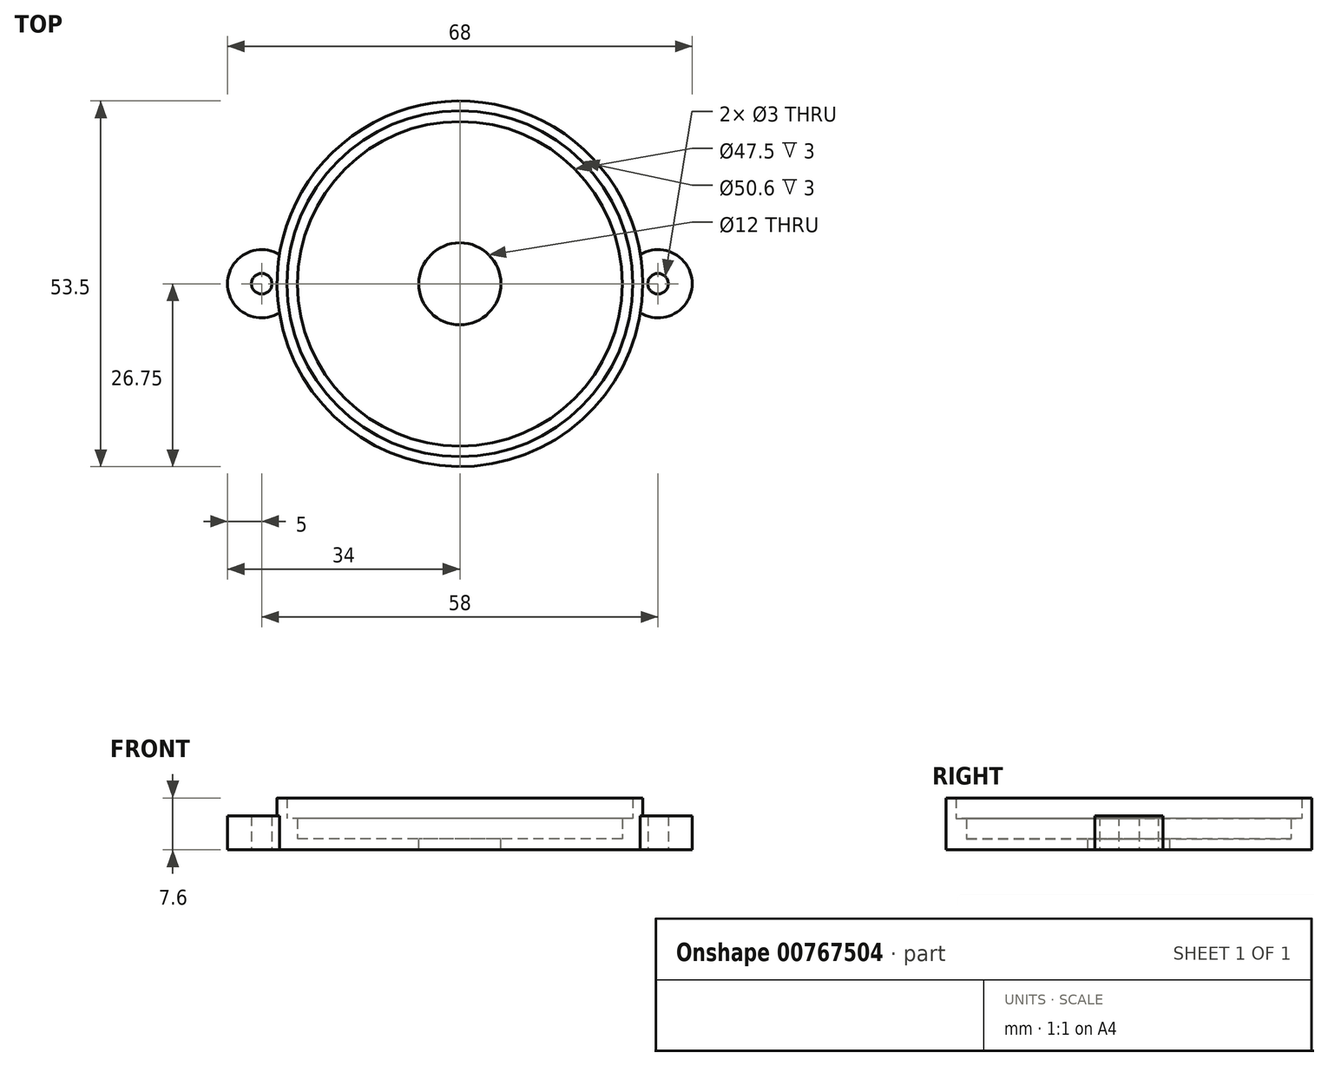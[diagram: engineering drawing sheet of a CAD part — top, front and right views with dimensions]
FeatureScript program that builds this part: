
annotation { "Feature Type Name" : "Feature", "Feature Type Description" : "" }
export const myFeature = defineFeature(function(context is Context, id is Id, definition is map)
    precondition{}
    {
        {
            var Q0;
            Q0=qCreatedBy(makeId("Top.planeOp"),FACE);
            var sketch = newSketch(context, id + "F0", { "sketchPlane" : qUnion([Q0])});
            skCircle(sketch, "E0", {"center": v(0, 0) * mm, "radius": 26.75 * mm});
            skSolve(sketch);
        }
        {
            var Q0;
            Q0=makeQuery(id+"F0.imprint","IMPRINT",FACE,{"disambiguationData":[TD([[makeQuery(id+"F0.imprint","IMPRINT",EDGE,{"derivedFrom":sQuery(id+"F0.wireOp",EDGE,"E0")}),1.0]])]});
            extrude(context, id + "F1", {"entities" : qUnion([Q0]), "depth" : 1.6 * mm, "offsetDistance" : 25 * mm});
        }
        {
            var Q0;
            Q0=makeQuery(id+"F1.opExtrude","CAP_FACE",FACE,{"disambiguationData":[OSD([sQuery(id+"F0.wireOp",EDGE,"E0")])],"isStart":false});
            var sketch = newSketch(context, id + "F2", { "sketchPlane" : qUnion([Q0])});
            skCircle(sketch, "E1", {"center": v(0, 0) * mm, "radius": 23.75 * mm});
            skSolve(sketch);
        }
        {
            var Q0;
            Q0=makeQuery(id+"F2.imprint","IMPRINT",FACE,{"disambiguationData":[TD([[makeQuery(id+"F2.imprint","IMPRINT",EDGE,{"derivedFrom":sQuery(id+"F2.wireOp",EDGE,"E1")}),-1.0]])]});
            extrude(context, id + "F3", {"entities" : qUnion([Q0]), "operationType" : NewBodyOperationType.ADD, "depth" : 3 * mm, "offsetDistance" : 25 * mm});
        }
        {
            var Q0;
            Q0=makeQuery(id+"F3.opExtrude","CAP_FACE",FACE,{"disambiguationData":[OSD([sQuery(id+"F0.wireOp",EDGE,"E0"),sQuery(id+"F2.wireOp",EDGE,"E1")])],"isStart":false});
            var sketch = newSketch(context, id + "F4", { "sketchPlane" : qUnion([Q0])});
            skCircle(sketch, "E2", {"center": v(0, 0) * mm, "radius": 25.3 * mm});
            skSolve(sketch);
        }
        {
            var Q0;
            Q0=makeQuery(id+"F4.imprint","IMPRINT",FACE,{"disambiguationData":[TD([[makeQuery(id+"F4.imprint","IMPRINT",EDGE,{"derivedFrom":sQuery(id+"F4.wireOp",EDGE,"E2")}),-1.0]])]});
            extrude(context, id + "F5", {"entities" : qUnion([Q0]), "operationType" : NewBodyOperationType.ADD, "depth" : 3 * mm, "offsetDistance" : 25 * mm});
        }
        {
            var Q0;
            Q0=makeQuery(id+"F1.opExtrude","CAP_FACE",FACE,{"disambiguationData":[OSD([sQuery(id+"F0.wireOp",EDGE,"E0")])],"isStart":false});
            var sketch = newSketch(context, id + "F6", { "sketchPlane" : qUnion([Q0])});
            skCircle(sketch, "E3", {"center": v(0, 0) * mm, "radius": 6 * mm});
            skSolve(sketch);
        }
        {
            var Q0;
            Q0=makeQuery(id+"F6.imprint","IMPRINT",FACE,{"disambiguationData":[TD([[makeQuery(id+"F6.imprint","IMPRINT",EDGE,{"derivedFrom":sQuery(id+"F6.wireOp",EDGE,"E3")}),1.0]])]});
            extrude(context, id + "F7", {"entities" : qUnion([Q0]), "operationType" : NewBodyOperationType.REMOVE, "oppositeDirection" : true, "depth" : 25 * mm, "offsetDistance" : 25 * mm});
        }
        {
            var Q0;
            Q0=qCreatedBy(makeId("Top.planeOp"),FACE);
            var sketch = newSketch(context, id + "F8", { "sketchPlane" : qUnion([Q0])});
            skCircle(sketch, "E4", {"center": v(29, 0) * mm, "radius": 5 * mm});
            skCircle(sketch, "E5", {"center": v(29, 0) * mm, "radius": 1.5 * mm});
            skCircle(sketch, "E6.1.0", {"center": v(-29, 0) * mm, "radius": 5 * mm});
            skCircle(sketch, "E6.1.1", {"center": v(-29, 0) * mm, "radius": 1.5 * mm});
            skPoint(sketch, "E6.center", {"position": v(0, 0) * mm});
            skCircle(sketch, "E7", {"center": v(0, 0) * mm, "radius": 26.75 * mm});
            skSolve(sketch);
        }
        {
            var Q0;
            Q0=makeQuery(id+"F8.imprint","IMPRINT",FACE,{"disambiguationData":[TD([[makeQuery(id+"F8.imprint","IMPRINT",EDGE,{"derivedFrom":sQuery(id+"F8.wireOp",EDGE,"E6.1.1")}),-1.0]])]});
            var Q1;
            Q1=makeQuery(id+"F8.imprint","IMPRINT",FACE,{"disambiguationData":[TD([[makeQuery(id+"F8.imprint","IMPRINT",EDGE,{"derivedFrom":sQuery(id+"F8.wireOp",EDGE,"E5")}),-1.0]])]});
            extrude(context, id + "F9", {"entities" : qUnion([Q0, Q1]), "operationType" : NewBodyOperationType.ADD, "depth" : 5 * mm, "offsetDistance" : 25 * mm});
        }
    });
